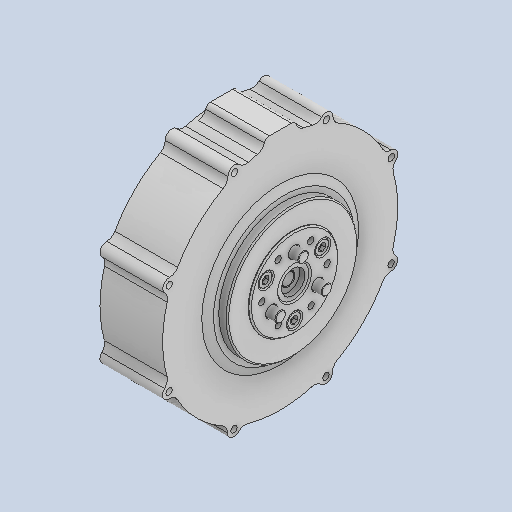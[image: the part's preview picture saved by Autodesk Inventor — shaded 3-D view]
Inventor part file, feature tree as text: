
AUTODESK INVENTOR PART (.ipt)
format: ipt  version: 2024.3 (Build 283343000, 343)  size: 909,312 bytes
history: native  units: mm
features: other x1, extrude x1, sketch x1
ambient origin geometry x8: Origin, YZ Plane, XZ Plane, XY Plane, X Axis, Y Axis, Z Axis, Center Point
bodies: 实体1 (feature_tree)
feature tree (3):
  other  "ソリッド1"
  extrude  "押し出し1"  Depth=3.0mm TaperAngle=0.0deg
  sketch  "スケッチ1"
